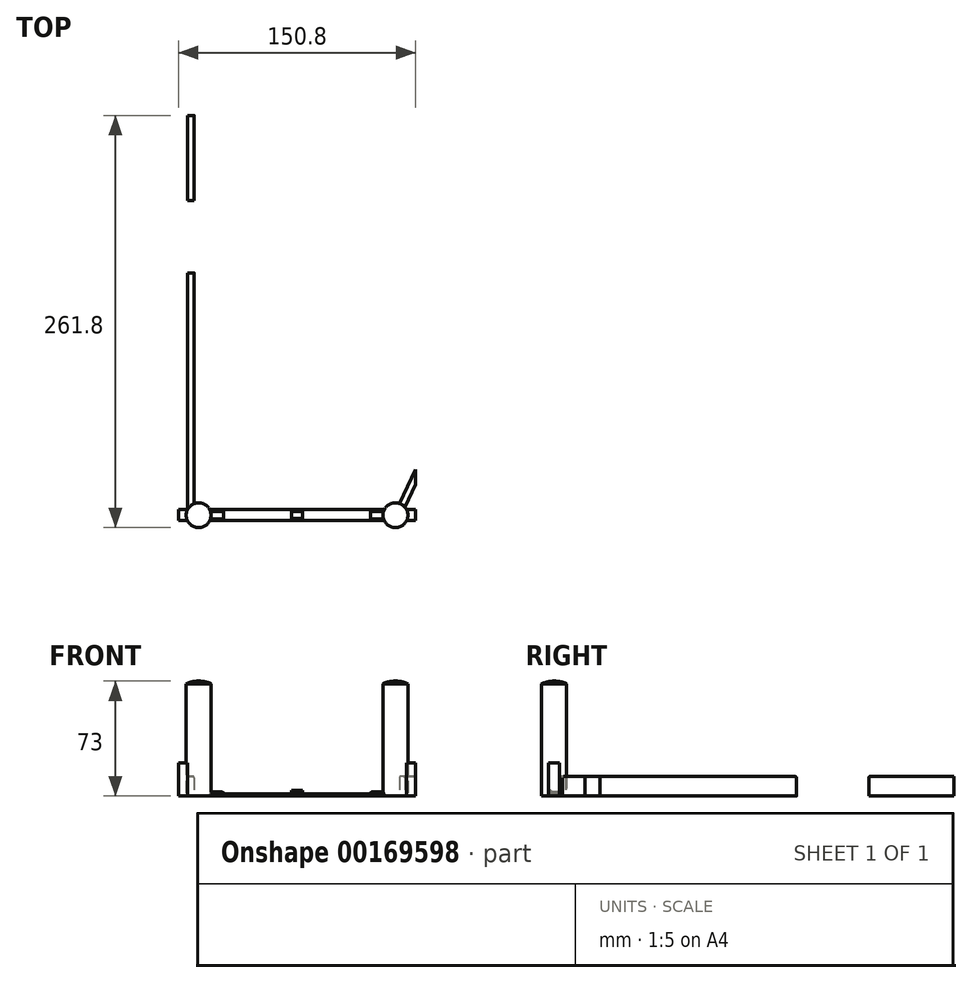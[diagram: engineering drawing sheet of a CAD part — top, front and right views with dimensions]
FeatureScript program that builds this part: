
annotation { "Feature Type Name" : "Feature", "Feature Type Description" : "" }
export const myFeature = defineFeature(function(context is Context, id is Id, definition is map)
    precondition{}
    {
        {
            var Q0;
            Q0=qCreatedBy(makeId("Top.planeOp"),FACE);
            var sketch = newSketch(context, id + "F0", { "sketchPlane" : qUnion([Q0])});
            skCircle(sketch, "E0", {"center": v(0, 0) * mm, "radius": 7.9 * mm});
            skCircle(sketch, "E1", {"center": v(125, 0) * mm, "radius": 7.9 * mm});
            skLineSegment(sketch, "E2", {"start": v(7.08, 3.5) * mm, "end": v(117.92, 3.5) * mm});
            skLineSegment(sketch, "E3", {"start": v(7.08, -3.5) * mm, "end": v(117.92, -3.5) * mm});
            skLineSegment(sketch, "E4", {"start": v(-7.08, 3.5) * mm, "end": v(-12.9, 3.5) * mm});
            skLineSegment(sketch, "E5", {"start": v(-12.9, 3.5) * mm, "end": v(-12.9, -3.5) * mm});
            skLineSegment(sketch, "E6", {"start": v(-12.9, -3.5) * mm, "end": v(-7.08, -3.5) * mm});
            skLineSegment(sketch, "E7", {"start": v(132.08, 3.5) * mm, "end": v(137.9, 3.5) * mm});
            skLineSegment(sketch, "E8", {"start": v(137.9, 3.5) * mm, "end": v(137.9, -3.5) * mm});
            skLineSegment(sketch, "E9", {"start": v(137.9, -3.5) * mm, "end": v(132.08, -3.5) * mm});
            skLineSegment(sketch, "E10", {"start": v(-7.08, 3.5) * mm, "end": v(-7.08, 153.9) * mm});
            skLineSegment(sketch, "E11", {"start": v(-7.08, 153.9) * mm, "end": v(-2.88, 153.9) * mm});
            skLineSegment(sketch, "E12", {"start": v(-2.88, 153.9) * mm, "end": v(-2.88, 7.36) * mm});
            skLineSegment(sketch, "E13", {"start": v(2.52, 1299.31) * mm, "end": v(16.73, 1299.31) * mm});
            skLineSegment(sketch, "E14", {"start": v(2.52, 1299.31) * mm, "end": v(2.52, 1304.24) * mm});
            skLineSegment(sketch, "E15", {"start": v(2.52, 1304.24) * mm, "end": v(2.52, 1299.31) * mm});
            skLineSegment(sketch, "E16", {"start": v(-7.08, 199.9) * mm, "end": v(-2.88, 199.9) * mm});
            skLineSegment(sketch, "E17", {"start": v(-2.88, 199.9) * mm, "end": v(-2.88, 253.9) * mm});
            skLineSegment(sketch, "E18", {"start": v(-2.88, 253.9) * mm, "end": v(-7.08, 253.9) * mm});
            skLineSegment(sketch, "E19", {"start": v(-7.08, 253.9) * mm, "end": v(-7.08, 199.9) * mm});
            skLineSegment(sketch, "E20", {"start": v(137.9, 19.5) * mm, "end": v(137.9, 29.16) * mm});
            skLineSegment(sketch, "E21", {"start": v(130.98, 5.17) * mm, "end": v(137.9, 19.5) * mm});
            skLineSegment(sketch, "E22", {"start": v(137.9, 29.16) * mm, "end": v(127.45, 7.51) * mm});
            skLineSegment(sketch, "E23.bottom", {"start": v(-7.08, 253.9) * mm, "end": v(137.9, 253.9) * mm});
            skLineSegment(sketch, "E23.top", {"start": v(-7.08, 265.9) * mm, "end": v(137.9, 265.9) * mm});
            skLineSegment(sketch, "E23.left", {"start": v(-7.08, 253.9) * mm, "end": v(-7.08, 265.9) * mm});
            skLineSegment(sketch, "E23.right", {"start": v(137.9, 253.9) * mm, "end": v(137.9, 265.9) * mm});
            skSolve(sketch);
        }
        {
            var Q0;
            {var subQ0=sQuery(id+"F0.wireOp",EDGE,"E10");Q0=makeQuery(id+"F0.imprint","IMPRINT",FACE,{"disambiguationData":[TD([[makeQuery(id+"F0.imprint","IMPRINT",EDGE,{"derivedFrom":subQ0}),-1.0]])]});}
            var Q1;
            Q1=makeQuery(id+"F0.imprint","IMPRINT",FACE,{"disambiguationData":[TD([[makeQuery(id+"F0.imprint","IMPRINT",EDGE,{"derivedFrom":sQuery(id+"F0.wireOp",EDGE,"E16")}),1.0]])]});
            var Q2;
            Q2=makeQuery(id+"F0.imprint","IMPRINT",FACE,{"disambiguationData":[TD([[makeQuery(id+"F0.imprint","IMPRINT",EDGE,{"derivedFrom":sQuery(id+"F0.wireOp",EDGE,"E20")}),1.0]])]});
            extrude(context, id + "F1", {"entities" : qUnion([Q0, Q1, Q2]), "depth" : 12.5 * mm});
        }
        {
            var Q0;
            {var subQ0=sQuery(id+"F0.wireOp",EDGE,"E4");Q0=makeQuery(id+"F0.imprint","IMPRINT",FACE,{"disambiguationData":[TD([[makeQuery(id+"F0.imprint","IMPRINT",EDGE,{"derivedFrom":subQ0}),1.0]])]});}
            var Q1;
            {var subQ0=sQuery(id+"F0.wireOp",EDGE,"E7");Q1=makeQuery(id+"F0.imprint","IMPRINT",FACE,{"disambiguationData":[TD([[makeQuery(id+"F0.imprint","IMPRINT",EDGE,{"derivedFrom":subQ0}),-1.0]])]});}
            extrude(context, id + "F2", {"entities" : qUnion([Q0, Q1]), "depth" : 21 * mm});
        }
        {
            var Q0;
            Q0=qCreatedBy(makeId("Right.planeOp"),FACE);
            var Q1;
            Q1=sQuery(id+"F0.wireOp",VERTEX,"E1.center");
            cPlane(context, id + "F3", {"entities" : qUnion([Q0, Q1]), "cplaneType" : CPlaneType.PLANE_POINT, "offset" : 25 * mm, "width" : 150 * mm, "height" : 150 * mm});
        }
        {
            var Q0;
            Q0=qCreatedBy(makeId("Right.planeOp"),FACE);
            var sketch = newSketch(context, id + "F4", { "sketchPlane" : qUnion([Q0])});
            skLineSegment(sketch, "E24", {"start": v(-7.9, 0) * mm, "end": v(-7.9, 71.37) * mm});
            skLineSegment(sketch, "E25", {"start": v(-7.9, 0) * mm, "end": v(0, 0) * mm});
            skLineSegment(sketch, "E26", {"start": v(0, 0) * mm, "end": v(0, 73) * mm});
            skArc(sketch, "E27", {"start": v(0, 73) * mm, "mid": v(-4.03, 72.59) * mm, "end": v(-7.9, 71.37) * mm});
            skSolve(sketch);
        }
        {
            var Q0;
            Q0=makeQuery(id+"F4.imprint","IMPRINT",FACE,{"disambiguationData":[TD([[makeQuery(id+"F4.imprint","IMPRINT",EDGE,{"derivedFrom":sQuery(id+"F4.wireOp",EDGE,"E24")}),-1.0]])]});
            var Q1;
            Q1=sQuery(id+"F4.wireOp",EDGE,"E26");
            revolve(context, id + "F5", {"entities" : qUnion([Q0]), "axis" : qUnion([Q1]), "revolveType" : RevolveType.FULL});
        }
        {
            var Q0;
            Q0=qCreatedBy(id+"F3.planeOp",FACE);
            var sketch = newSketch(context, id + "F6", { "sketchPlane" : qUnion([Q0])});
            skLineSegment(sketch, "E28", {"start": v(0, 0) * mm, "end": v(0, 73) * mm});
            skLineSegment(sketch, "E29", {"start": v(0, 0) * mm, "end": v(-7.9, 0) * mm});
            skLineSegment(sketch, "E30", {"start": v(-7.9, 0) * mm, "end": v(-7.9, 71.37) * mm});
            skArc(sketch, "E31", {"start": v(0, 73) * mm, "mid": v(-4.03, 72.59) * mm, "end": v(-7.9, 71.37) * mm});
            skSolve(sketch);
        }
        {
            var Q0;
            Q0=makeQuery(id+"F6.imprint","IMPRINT",FACE,{"disambiguationData":[TD([[makeQuery(id+"F6.imprint","IMPRINT",EDGE,{"derivedFrom":sQuery(id+"F6.wireOp",EDGE,"E28")}),1.0]])]});
            var Q1;
            Q1=sQuery(id+"F6.wireOp",EDGE,"E28");
            revolve(context, id + "F7", {"entities" : qUnion([Q0]), "axis" : qUnion([Q1]), "revolveType" : RevolveType.FULL});
        }
        {
            var Q0;
            {var subQ0=sQuery(id+"F0.wireOp",EDGE,"E2");Q0=makeQuery(id+"F0.imprint","IMPRINT",FACE,{"disambiguationData":[TD([[makeQuery(id+"F0.imprint","IMPRINT",EDGE,{"derivedFrom":subQ0}),-1.0]])]});}
            extrude(context, id + "F8", {"entities" : qUnion([Q0]), "depth" : 1.5 * mm});
        }
        {
            var Q0;
            Q0=makeQuery(id+"F8.opExtrude","CAP_EDGE",EDGE,{"disambiguationData":[OSD([sQuery(id+"F0.wireOp",EDGE,"E3")])],"isStart":false});
            var Q1;
            Q1=makeQuery(id+"F8.opExtrude","CAP_EDGE",EDGE,{"disambiguationData":[OSD([sQuery(id+"F0.wireOp",EDGE,"E2")])],"isStart":false});
            fillet(context, id + "F9", {"entities" : qUnion([Q0, Q1]), "radius" : 1 * mm, "tangentPropagation" : true, "allowEdgeOverflow" : false});
        }
        {
            var Q0;
            Q0=makeQuery(id+"F8.opExtrude","CAP_FACE",FACE,{"disambiguationData":[OSD([sQuery(id+"F0.wireOp",EDGE,"E0"),sQuery(id+"F0.wireOp",EDGE,"E1"),sQuery(id+"F0.wireOp",EDGE,"E2"),sQuery(id+"F0.wireOp",EDGE,"E3")])],"isStart":false});
            var sketch = newSketch(context, id + "F10", { "sketchPlane" : qUnion([Q0])});
            skLineSegment(sketch, "E32", {"start": v(7.5, 2.5) * mm, "end": v(15.9, 2.5) * mm});
            skLineSegment(sketch, "E33", {"start": v(15.9, 2.5) * mm, "end": v(15.9, -2.5) * mm});
            skLineSegment(sketch, "E34", {"start": v(15.9, -2.5) * mm, "end": v(7.5, -2.5) * mm});
            skLineSegment(sketch, "E35", {"start": v(117.5, 2.5) * mm, "end": v(109.1, 2.5) * mm});
            skLineSegment(sketch, "E36", {"start": v(109.1, 2.5) * mm, "end": v(109.1, -2.5) * mm});
            skLineSegment(sketch, "E37", {"start": v(109.1, -2.5) * mm, "end": v(117.5, -2.5) * mm});
            skArc(sketch, "E38", {"start": v(117.5, 2.5) * mm, "mid": v(117.1, 0) * mm, "end": v(117.5, -2.5) * mm});
            skLineSegment(sketch, "E39.bottom", {"start": v(58.9, 2.5) * mm, "end": v(66.1, 2.5) * mm});
            skLineSegment(sketch, "E39.top", {"start": v(58.9, -2.5) * mm, "end": v(66.1, -2.5) * mm});
            skLineSegment(sketch, "E39.left", {"start": v(58.9, 2.5) * mm, "end": v(58.9, -2.5) * mm});
            skLineSegment(sketch, "E39.right", {"start": v(66.1, 2.5) * mm, "end": v(66.1, -2.5) * mm});
            skSolve(sketch);
        }
        {
            var Q0;
            Q0=makeQuery(id+"F10.imprint","IMPRINT",FACE,{"disambiguationData":[TD([[makeQuery(id+"F10.imprint","IMPRINT",EDGE,{"derivedFrom":sQuery(id+"F10.wireOp",EDGE,"E32")}),1.0]])]});
            var Q1;
            Q1=makeQuery(id+"F10.imprint","IMPRINT",FACE,{"disambiguationData":[TD([[makeQuery(id+"F10.imprint","IMPRINT",EDGE,{"derivedFrom":sQuery(id+"F10.wireOp",EDGE,"E35")}),1.0]])]});
            var Q2;
            Q2=makeQuery(id+"F10.imprint","IMPRINT",FACE,{"disambiguationData":[TD([[makeQuery(id+"F10.imprint","IMPRINT",EDGE,{"derivedFrom":sQuery(id+"F10.wireOp",EDGE,"E39.bottom")}),1.0]])]});
            extrude(context, id + "F11", {"entities" : qUnion([Q0, Q1, Q2]), "depth" : 1 * mm, "offsetDistance" : 25 * mm});
        }
        {
            var Q0;
            Q0=makeQuery(id+"F11.opExtrude","CAP_EDGE",EDGE,{"disambiguationData":[OSD([sQuery(id+"F10.wireOp",EDGE,"E34")])],"isStart":false});
            var Q1;
            Q1=makeQuery(id+"F11.opExtrude","CAP_EDGE",EDGE,{"disambiguationData":[OSD([sQuery(id+"F10.wireOp",EDGE,"E33")])],"isStart":false});
            var Q2;
            Q2=makeQuery(id+"F11.opExtrude","CAP_EDGE",EDGE,{"disambiguationData":[OSD([sQuery(id+"F10.wireOp",EDGE,"E32")])],"isStart":false});
            var Q3;
            Q3=makeQuery(id+"F11.opExtrude","CAP_EDGE",EDGE,{"disambiguationData":[OSD([sQuery(id+"F10.wireOp",EDGE,"E37")])],"isStart":false});
            var Q4;
            Q4=makeQuery(id+"F11.opExtrude","CAP_EDGE",EDGE,{"disambiguationData":[OSD([sQuery(id+"F10.wireOp",EDGE,"E36")])],"isStart":false});
            var Q5;
            Q5=makeQuery(id+"F11.opExtrude","CAP_EDGE",EDGE,{"disambiguationData":[OSD([sQuery(id+"F10.wireOp",EDGE,"E35")])],"isStart":false});
            fillet(context, id + "F12", {"entities" : qUnion([Q0, Q1, Q2, Q3, Q4, Q5]), "radius" : 1 * mm, "tangentPropagation" : true, "allowEdgeOverflow" : false});
        }
        {
            var Q0;
            Q0=makeQuery(id+"F1.opExtrude","CAP_EDGE",EDGE,{"disambiguationData":[OSD([sQuery(id+"F0.wireOp",EDGE,"E12")])],"isStart":false});
            var Q1;
            Q1=makeQuery(id+"F1.opExtrude","CAP_EDGE",EDGE,{"disambiguationData":[OSD([sQuery(id+"F0.wireOp",EDGE,"E10")])],"isStart":false});
            var Q2;
            Q2=makeQuery(id+"F1.opExtrude","CAP_EDGE",EDGE,{"disambiguationData":[OSD([sQuery(id+"F0.wireOp",EDGE,"E17")])],"isStart":false});
            var Q3;
            Q3=makeQuery(id+"F1.opExtrude","CAP_EDGE",EDGE,{"disambiguationData":[OSD([sQuery(id+"F0.wireOp",EDGE,"E19")])],"isStart":false});
            var Q4;
            Q4=makeQuery(id+"F1.opExtrude","CAP_EDGE",EDGE,{"disambiguationData":[OSD([sQuery(id+"F0.wireOp",EDGE,"E12")])],"isStart":true});
            var Q5;
            Q5=makeQuery(id+"F1.opExtrude","CAP_EDGE",EDGE,{"disambiguationData":[OSD([sQuery(id+"F0.wireOp",EDGE,"E16")])],"isStart":false});
            var Q6;
            Q6=makeQuery(id+"F1.opExtrude","CAP_EDGE",EDGE,{"disambiguationData":[OSD([sQuery(id+"F0.wireOp",EDGE,"E11")])],"isStart":false});
            var Q7;
            Q7=makeQuery(id+"F1.opExtrude","CAP_EDGE",EDGE,{"disambiguationData":[OSD([sQuery(id+"F0.wireOp",EDGE,"E21")])],"isStart":false});
            var Q8;
            Q8=makeQuery(id+"F1.opExtrude","CAP_EDGE",EDGE,{"disambiguationData":[OSD([sQuery(id+"F0.wireOp",EDGE,"E22")])],"isStart":false});
            fillet(context, id + "F13", {"entities" : qUnion([Q0, Q1, Q2, Q3, Q4, Q5, Q6, Q7, Q8]), "radius" : 1 * mm, "tangentPropagation" : true, "allowEdgeOverflow" : false});
        }
        {
            var Q0;
            Q0=makeQuery(id+"F11.opExtrude","CAP_FACE",FACE,{"disambiguationData":[OSD([sQuery(id+"F10.wireOp",EDGE,"E39.bottom"),sQuery(id+"F10.wireOp",EDGE,"E39.top"),sQuery(id+"F10.wireOp",EDGE,"E39.left"),sQuery(id+"F10.wireOp",EDGE,"E39.right")])],"isStart":false});
            var sketch = newSketch(context, id + "F14", { "sketchPlane" : qUnion([Q0])});
            skLineSegment(sketch, "E40.bottom", {"start": v(58.9, -2.5) * mm, "end": v(66.1, -2.5) * mm});
            skLineSegment(sketch, "E40.top", {"start": v(58.9, -2) * mm, "end": v(66.1, -2) * mm});
            skLineSegment(sketch, "E40.left", {"start": v(58.9, -2.5) * mm, "end": v(58.9, -2) * mm});
            skLineSegment(sketch, "E40.right", {"start": v(66.1, -2.5) * mm, "end": v(66.1, -2) * mm});
            skSolve(sketch);
        }
        {
            var Q0;
            Q0=makeQuery(id+"F14.imprint","IMPRINT",FACE,{"disambiguationData":[TD([[makeQuery(id+"F14.imprint","IMPRINT",EDGE,{"derivedFrom":sQuery(id+"F14.wireOp",EDGE,"E40.bottom")}),1.0]])]});
            extrude(context, id + "F15", {"entities" : qUnion([Q0]), "operationType" : NewBodyOperationType.ADD, "depth" : 1 * mm, "offsetDistance" : 25 * mm});
        }
    });
